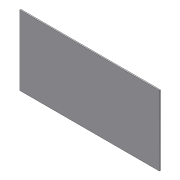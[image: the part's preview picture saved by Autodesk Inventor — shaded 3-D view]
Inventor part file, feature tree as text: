
AUTODESK INVENTOR PART (.ipt)
format: ipt  version: 2012 (Build 160160000, 160)  size: 62,976 bytes
history: native  units: in
note: dims shown in document units (in); Inventor stores cm internally (conversion verified against a paired STEP export)
features: extrude x1, sketch x1
ambient origin geometry x8: Origin, YZ Plane, XZ Plane, XY Plane, X Axis, Y Axis, Z Axis, Center Point
bodies: Solid1 (feature_tree)
feature tree (2):
  extrude  "Extrusion1"  Depth=8.0in
  sketch  "Sketch1"  dims[d0=16.0in d1=8.0in d2=0.125in d3=0.0in]
